# Revit family: Toilet_Elongated-Siphonic_Dual_Flush-American_Standard-H2OPTION-2887_Series
name_source: partatom
category: Plumbing Fixtures
revit_build: Autodesk Revit 2014 (Build: 20130308_1515(x64)
units: mm (PartAtom-declared; Revit-internal decimal feet)

## types (4) — shared parameters
Assembly Code = D2010110
Bowl Shape = Elongated
CW Connection = Yes
CWFU = 5
Cold Water Connection Diameter = 1/2"
Cold Water Connection Radius = 1/4"
Default Elevation = 0"
HW Connection = No
Height = 30"
Installation Type = Floor Mounted
Length = 29 3/4"
Manufacturer = American Standard
Material = Vitreous China-American Standard-020-White
Price = Prices may vary. Please consult Manufacturer Representative for most up-to-date price list.
Product Documentation Link = https://www.americanstandard-us.com
Product Page URL = https://www.americanstandard-us.com
Revised Date = 02/22/2017
URL = http://www.americanstandard-us.com
Vent Connection = No
WFU = 5
Warranty Information = 5 Years Limited
Waste Connection = Yes
Waste Connection Diameter = 2"
Waste Connection Radius = 1"
Width = 15"
zero-valued in all types: HWFU

## per-type parameters (varying)
| type | Aquaguard Liner | Description | Flush Rate | Lined Tank | Type Comments |
| 2887.218 | No | H2Option Siphonic Dual Flush Elongated Toilet. | Full Flush (4.8 Lpf/1.28gpf) or Partial Flush (3.4 Lpf/0.92 gpf) | No |  |
| 2887.518 | Yes | H2Option Siphonic Dual Flush Elongated Toilet. | Full Flush (4.8 Lpf/1.28gpf) or Partial Flush (3.4 Lpf/0.92 gpf) | No | 2887.518 Same as 2887.218, except with Tank with AquaGuard Liner. |
| 2887.216 | No | H2Option Dual Flush Elongated Toilet. | Full Flush (6.0 Lpf/1.3 gpf) or Partial Flush (3.8 Lpf/0.84 gpf) | No |  |
| 2887.516 | No | H2Option Dual Flush Elongated Toilet. | Full Flush (6.0 Lpf/1.3 gpf) or Partial Flush (3.8 Lpf/0.84 gpf) | Yes | 2887.516 Same as 2887.216, except with Lined Tank. |

note: column(s) folded — value = type name in every type: Model

## geometry (parser evidence)
native form markers: Sweep x1
no freeform markers — native parametric forms only
